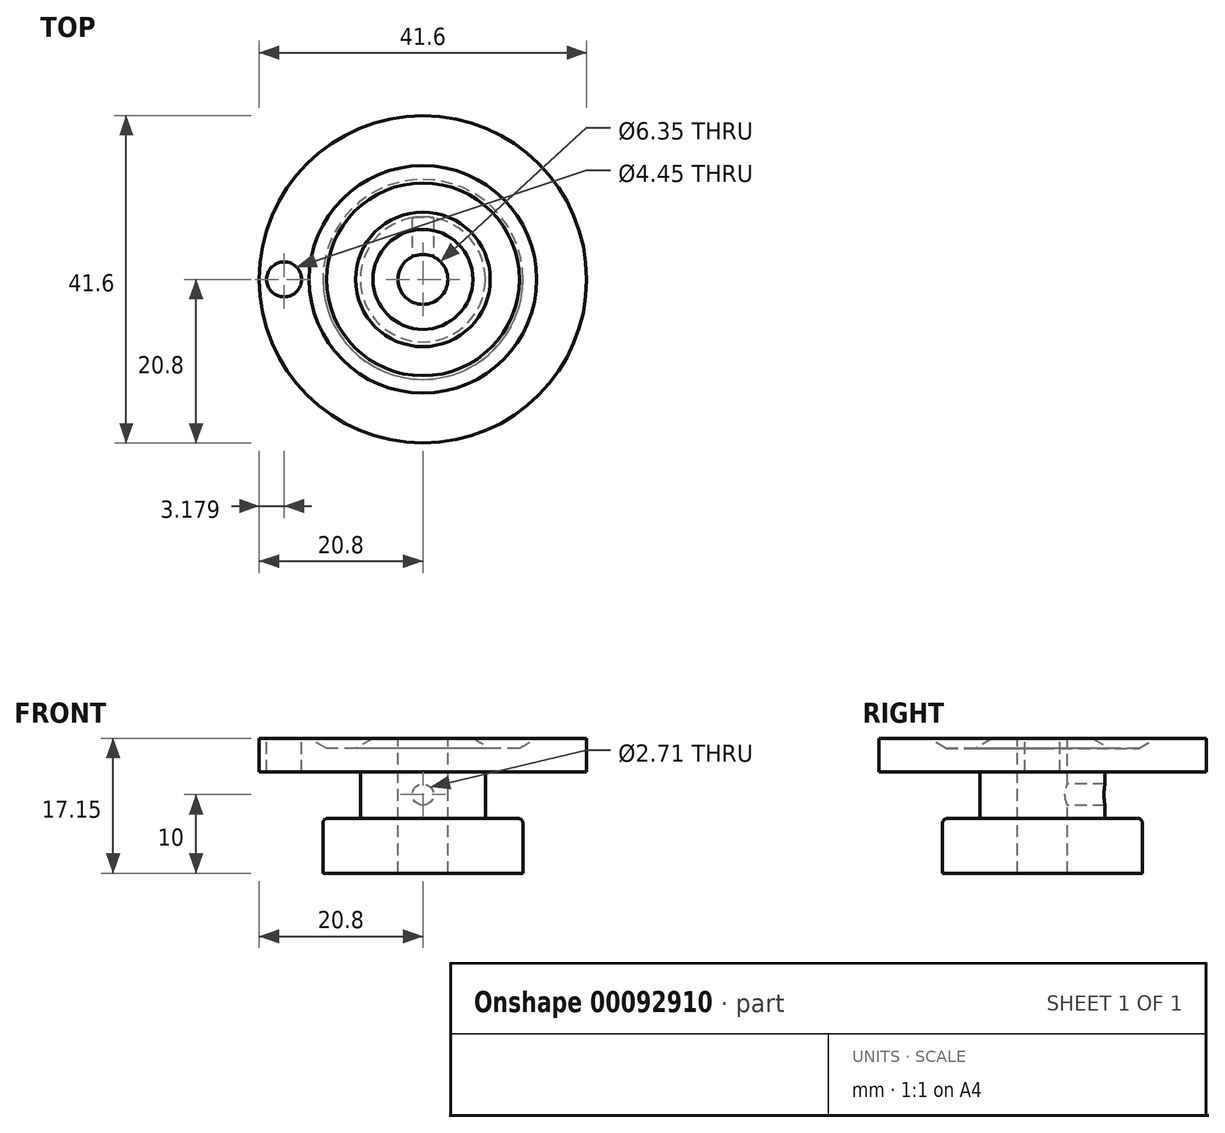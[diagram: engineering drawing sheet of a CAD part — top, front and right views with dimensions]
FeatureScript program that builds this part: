
annotation { "Feature Type Name" : "Feature", "Feature Type Description" : "" }
export const myFeature = defineFeature(function(context is Context, id is Id, definition is map)
    precondition{}
    {
        {
            var Q0;
            Q0=qCreatedBy(makeId("Front.planeOp"),FACE);
            var sketch = newSketch(context, id + "F0", { "sketchPlane" : qUnion([Q0])});
            skLineSegment(sketch, "E0", {"start": v(0, 0) * mm, "end": v(-12.7, 0) * mm});
            skLineSegment(sketch, "E1", {"start": v(-12.7, 0) * mm, "end": v(-12.7, 6.99) * mm});
            skLineSegment(sketch, "E2", {"start": v(-12.7, 6.99) * mm, "end": v(-7.94, 6.99) * mm});
            skLineSegment(sketch, "E3", {"start": v(-7.94, 6.99) * mm, "end": v(-7.94, 12.9) * mm});
            skLineSegment(sketch, "E4", {"start": v(-7.94, 12.9) * mm, "end": v(-20.8, 12.9) * mm});
            skLineSegment(sketch, "E5", {"start": v(-20.8, 12.9) * mm, "end": v(-20.8, 17.15) * mm});
            skLineSegment(sketch, "E6", {"start": v(-20.8, 17.15) * mm, "end": v(-14.45, 17.15) * mm});
            skLineSegment(sketch, "E7", {"start": v(-14.45, 17.15) * mm, "end": v(-12.25, 15.88) * mm});
            skLineSegment(sketch, "E8", {"start": v(-12.25, 15.88) * mm, "end": v(-8.55, 15.88) * mm});
            skLineSegment(sketch, "E9", {"start": v(-8.55, 15.88) * mm, "end": v(-6.35, 17.15) * mm});
            skLineSegment(sketch, "E10", {"start": v(-6.35, 17.15) * mm, "end": v(0, 17.15) * mm});
            skLineSegment(sketch, "E11", {"start": v(0, 17.15) * mm, "end": v(0, 0) * mm});
            skPoint(sketch, "E12", {"position": v(0, 10) * mm});
            skSolve(sketch);
        }
        {
            var Q0;
            Q0=makeQuery(id+"F0.imprint","IMPRINT",FACE,{"disambiguationData":[TD([[makeQuery(id+"F0.imprint","IMPRINT",EDGE,{"derivedFrom":sQuery(id+"F0.wireOp",EDGE,"E0")}),-1.0]])]});
            var Q1;
            Q1=sQuery(id+"F0.wireOp",EDGE,"E11");
            revolve(context, id + "F1", {"entities" : qUnion([Q0]), "axis" : qUnion([Q1]), "revolveType" : RevolveType.FULL});
        }
        {
            var Q0;
            Q0=makeQuery(id+"F1.opRevolve","SWEPT_EDGE",EDGE,{"disambiguationData":[OSD([sQuery(id+"F0.wireOp",EDGE,"E1"),sQuery(id+"F0.wireOp",EDGE,"E2")])]});
            fillet(context, id + "F2", {"entities" : qUnion([Q0]), "radius" : 0.64 * mm, "tangentPropagation" : true, "allowEdgeOverflow" : false});
        }
        {
            var Q0;
            Q0=makeQuery(id+"F1.opRevolve","SWEPT_FACE",FACE,{"disambiguationData":[OSD([sQuery(id+"F0.wireOp",EDGE,"E10")])]});
            var sketch = newSketch(context, id + "F3", { "sketchPlane" : qUnion([Q0])});
            skPoint(sketch, "E13", {"position": v(0, 0) * mm});
            skSolve(sketch);
        }
        {
            var Q0;
            Q0=sQuery(id+"F3.wireOp",VERTEX,"E13");
            var Q1;
            Q1=makeQuery(id+"F1.opRevolve","SWEPT_BODY",BODY,{"disambiguationData":[OSD([sQuery(id+"F0.wireOp",EDGE,"E0"),sQuery(id+"F0.wireOp",EDGE,"E1"),sQuery(id+"F0.wireOp",EDGE,"E2"),sQuery(id+"F0.wireOp",EDGE,"E3"),sQuery(id+"F0.wireOp",EDGE,"E4"),sQuery(id+"F0.wireOp",EDGE,"E5"),sQuery(id+"F0.wireOp",EDGE,"E6"),sQuery(id+"F0.wireOp",EDGE,"E7"),sQuery(id+"F0.wireOp",EDGE,"E8"),sQuery(id+"F0.wireOp",EDGE,"E9"),sQuery(id+"F0.wireOp",EDGE,"E10"),sQuery(id+"F0.wireOp",EDGE,"E11")])]});
            hole(context, id + "F4", {"style" : HoleStyle.SIMPLE, "holeDiameter" : 6.35 * mm, "endStyle" : HoleEndStyle.THROUGH, "locations" : qUnion([Q0]), "scope" : qUnion([Q1])});
        }
        {
            var Q0;
            Q0=makeQuery(id+"F1.opRevolve","SWEPT_FACE",FACE,{"disambiguationData":[OSD([sQuery(id+"F0.wireOp",EDGE,"E6")])]});
            var sketch = newSketch(context, id + "F5", { "sketchPlane" : qUnion([Q0])});
            skLineSegment(sketch, "E14", {"start": v(-20.8, 0) * mm, "end": v(-17.62, 0) * mm, "construction": true});
            skLineSegment(sketch, "E15", {"start": v(-17.62, 0) * mm, "end": v(-14.45, 0) * mm, "construction": true});
            skSolve(sketch);
        }
        {
            var Q0;
            Q0=sQuery(id+"F5.wireOp",VERTEX,"E15.start");
            var Q1;
            Q1=makeQuery(id+"F1.opRevolve","SWEPT_BODY",BODY,{"disambiguationData":[OSD([sQuery(id+"F0.wireOp",EDGE,"E0"),sQuery(id+"F0.wireOp",EDGE,"E1"),sQuery(id+"F0.wireOp",EDGE,"E2"),sQuery(id+"F0.wireOp",EDGE,"E3"),sQuery(id+"F0.wireOp",EDGE,"E4"),sQuery(id+"F0.wireOp",EDGE,"E5"),sQuery(id+"F0.wireOp",EDGE,"E6"),sQuery(id+"F0.wireOp",EDGE,"E7"),sQuery(id+"F0.wireOp",EDGE,"E8"),sQuery(id+"F0.wireOp",EDGE,"E9"),sQuery(id+"F0.wireOp",EDGE,"E10"),sQuery(id+"F0.wireOp",EDGE,"E11")])]});
            hole(context, id + "F6", {"style" : HoleStyle.SIMPLE, "holeDiameter" : 4.44 * mm, "endStyle" : HoleEndStyle.THROUGH, "locations" : qUnion([Q0]), "scope" : qUnion([Q1])});
        }
        {
            var Q0;
            Q0=sQuery(id+"F0.wireOp",VERTEX,"E12");
            var Q1;
            Q1=makeQuery(id+"F1.opRevolve","SWEPT_BODY",BODY,{"disambiguationData":[OSD([sQuery(id+"F0.wireOp",EDGE,"E0"),sQuery(id+"F0.wireOp",EDGE,"E1"),sQuery(id+"F0.wireOp",EDGE,"E2"),sQuery(id+"F0.wireOp",EDGE,"E3"),sQuery(id+"F0.wireOp",EDGE,"E4"),sQuery(id+"F0.wireOp",EDGE,"E5"),sQuery(id+"F0.wireOp",EDGE,"E6"),sQuery(id+"F0.wireOp",EDGE,"E7"),sQuery(id+"F0.wireOp",EDGE,"E8"),sQuery(id+"F0.wireOp",EDGE,"E9"),sQuery(id+"F0.wireOp",EDGE,"E10"),sQuery(id+"F0.wireOp",EDGE,"E11")])]});
            hole(context, id + "F7", {"style" : HoleStyle.SIMPLE, "endStyle" : HoleEndStyle.THROUGH, "standardTappedOrClearance" : lookupTablePath({ "standard" : "ANSI", "engagement" : "75%", "pitch" : "32 tpi", "size" : "#6", "type" : "Tapped" }), "standardBlindInLast" : lookupTablePath({ "standard" : "ANSI", "engagement" : "75%", "pitch" : "32 tpi", "size" : "#6", "type" : "Tapped" }), "holeDiameter" : 2.7 * mm, "locations" : qUnion([Q0]), "scope" : qUnion([Q1]), "isTappedThrough" : true, "majorDiameter" : 3.5 * mm, "showTappedDepth" : true});
        }
    });
